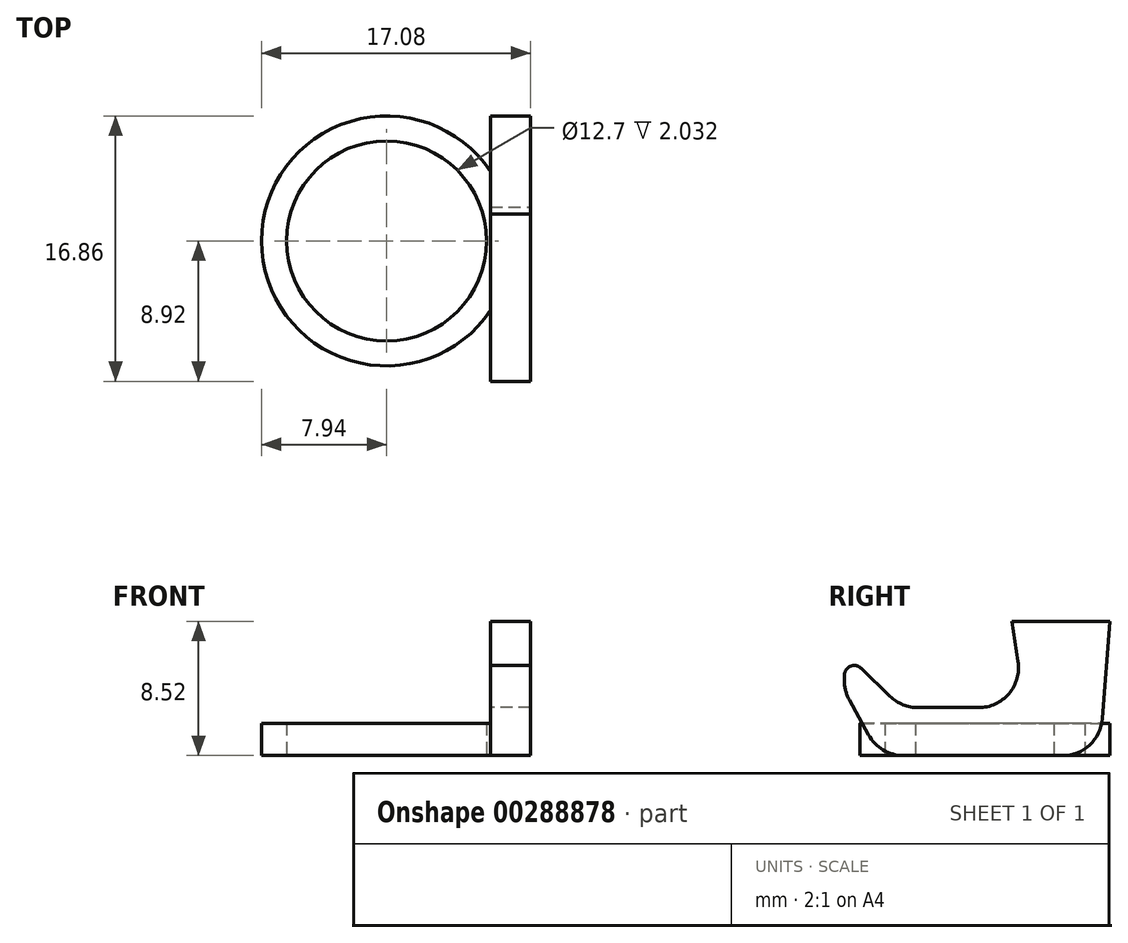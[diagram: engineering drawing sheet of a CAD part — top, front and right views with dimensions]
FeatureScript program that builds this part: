
annotation { "Feature Type Name" : "Feature", "Feature Type Description" : "" }
export const myFeature = defineFeature(function(context is Context, id is Id, definition is map)
    precondition{}
    {
        {
            var Q0;
            Q0=qCreatedBy(makeId("Top.planeOp"),FACE);
            var sketch = newSketch(context, id + "F0", { "sketchPlane" : qUnion([Q0])});
            skCircle(sketch, "E0", {"center": v(0, 0) * mm, "radius": 6.35 * mm});
            skCircle(sketch, "E1", {"center": v(0, 0) * mm, "radius": 7.94 * mm});
            skSolve(sketch);
        }
        {
            var Q0;
            Q0 = qSketchRegion(id + "F0", true);
            extrude(context, id + "F1", {"entities" : qUnion([Q0]), "depth" : 2.03 * mm});
        }
        {
            var Q0;
            Q0=qCreatedBy(makeId("Right.planeOp"),FACE);
            cPlane(context, id + "F2", {"entities" : qUnion([Q0]), "cplaneType" : CPlaneType.OFFSET, "offset" : 7.87 * mm, "width" : 152.4 * mm, "height" : 152.4 * mm});
        }
        {
            var Q0;
            Q0=qCreatedBy(id+"F2.planeOp",FACE);
            var sketch = newSketch(context, id + "F3", { "sketchPlane" : qUnion([Q0])});
            skLineSegment(sketch, "E2", {"start": v(7.3, 0) * mm, "end": v(-6.67, 0) * mm});
            skLineSegment(sketch, "E3", {"start": v(-6.67, 0) * mm, "end": v(-8.92, 4.12) * mm});
            skLineSegment(sketch, "E4", {"start": v(-8.92, 4.12) * mm, "end": v(-8.92, 6.59) * mm});
            skLineSegment(sketch, "E5", {"start": v(-8.92, 6.59) * mm, "end": v(-5.27, 3.05) * mm});
            skLineSegment(sketch, "E6", {"start": v(-5.27, 3.05) * mm, "end": v(2.57, 3.05) * mm});
            skLineSegment(sketch, "E7", {"start": v(2.57, 3.05) * mm, "end": v(1.72, 8.52) * mm});
            skLineSegment(sketch, "E8", {"start": v(1.72, 8.52) * mm, "end": v(7.93, 8.52) * mm});
            skLineSegment(sketch, "E9", {"start": v(7.93, 8.52) * mm, "end": v(7.3, 0) * mm});
            skSolve(sketch);
        }
        {
            var Q0;
            Q0 = qSketchRegion(id + "F3", true);
            extrude(context, id + "F4", {"entities" : qUnion([Q0]), "operationType" : NewBodyOperationType.ADD, "endBound" : BoundingType.SYMMETRIC, "depth" : 2.54 * mm});
        }
        {
            var Q0;
            Q0=makeQuery(id+"F4.opExtrude","SWEPT_EDGE",EDGE,{"disambiguationData":[OSD([sQuery(id+"F3.wireOp",EDGE,"E6"),sQuery(id+"F3.wireOp",EDGE,"E7")])]});
            var Q1;
            Q1=makeQuery(id+"F4.opExtrude","SWEPT_EDGE",EDGE,{"disambiguationData":[OSD([sQuery(id+"F3.wireOp",EDGE,"E5"),sQuery(id+"F3.wireOp",EDGE,"E6")])]});
            var Q2;
            Q2=makeQuery(id+"F4.opExtrude","SWEPT_EDGE",EDGE,{"disambiguationData":[OSD([sQuery(id+"F3.wireOp",EDGE,"E2"),sQuery(id+"F3.wireOp",EDGE,"E9")])]});
            var Q3;
            Q3=makeQuery(id+"F4.opExtrude","SWEPT_EDGE",EDGE,{"disambiguationData":[OSD([sQuery(id+"F3.wireOp",EDGE,"E2"),sQuery(id+"F3.wireOp",EDGE,"E3")])]});
            var Q4;
            Q4=makeQuery(id+"F4.opExtrude","SWEPT_EDGE",EDGE,{"disambiguationData":[OSD([sQuery(id+"F3.wireOp",EDGE,"E3"),sQuery(id+"F3.wireOp",EDGE,"E4")])]});
            fillet(context, id + "F5", {"entities" : qUnion([Q0, Q1, Q2, Q3, Q4]), "radius" : 2.54 * mm, "tangentPropagation" : true, "allowEdgeOverflow" : false});
        }
        {
            var Q0;
            Q0=makeQuery(id+"F4.opExtrude","SWEPT_EDGE",EDGE,{"disambiguationData":[OSD([sQuery(id+"F3.wireOp",EDGE,"E4"),sQuery(id+"F3.wireOp",EDGE,"E5")])]});
            fillet(context, id + "F6", {"entities" : qUnion([Q0]), "radius" : 0.64 * mm, "tangentPropagation" : true, "allowEdgeOverflow" : false});
        }
    });
